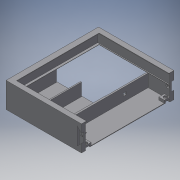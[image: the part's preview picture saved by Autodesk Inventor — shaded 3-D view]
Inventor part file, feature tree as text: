
AUTODESK INVENTOR PART (.ipt)
format: ipt  version: 2016 SP2 (Build 200236200, 236)  size: 300,544 bytes
history: native  units: mm
features: sketch x22, other x3
ambient origin geometry x8: Origin, YZ Plane, XZ Plane, XY Plane, X Axis, Y Axis, Z Axis, Center Point
bodies: Volumenkörper1 (feature_tree)
feature tree (25):
  other  "Bauteil1.ipt"
  other  "Volumenkörper1::Bauteil1.ipt"
  other  "Bezeichnung1"
  sketch  "Skizze1"  dims[d0=10.0mm]
  sketch  "Skizze2"
  sketch  "Skizze3"
  sketch  "Skizze4"
  sketch  "Skizze5"
  sketch  "Skizze6"
  sketch  "Skizze7"
  sketch  "Skizze8"
  sketch  "Skizze9"
  sketch  "Skizze10"
  sketch  "Skizze11"
  sketch  "Skizze13"
  sketch  "Skizze14"
  sketch  "Skizze15"
  sketch  "Skizze16"
  sketch  "Skizze17"
  sketch  "Skizze19"
  sketch  "Skizze21"
  sketch  "Skizze22"
  sketch  "Skizze23"
  sketch  "Skizze24"
  sketch  "Skizze25"
